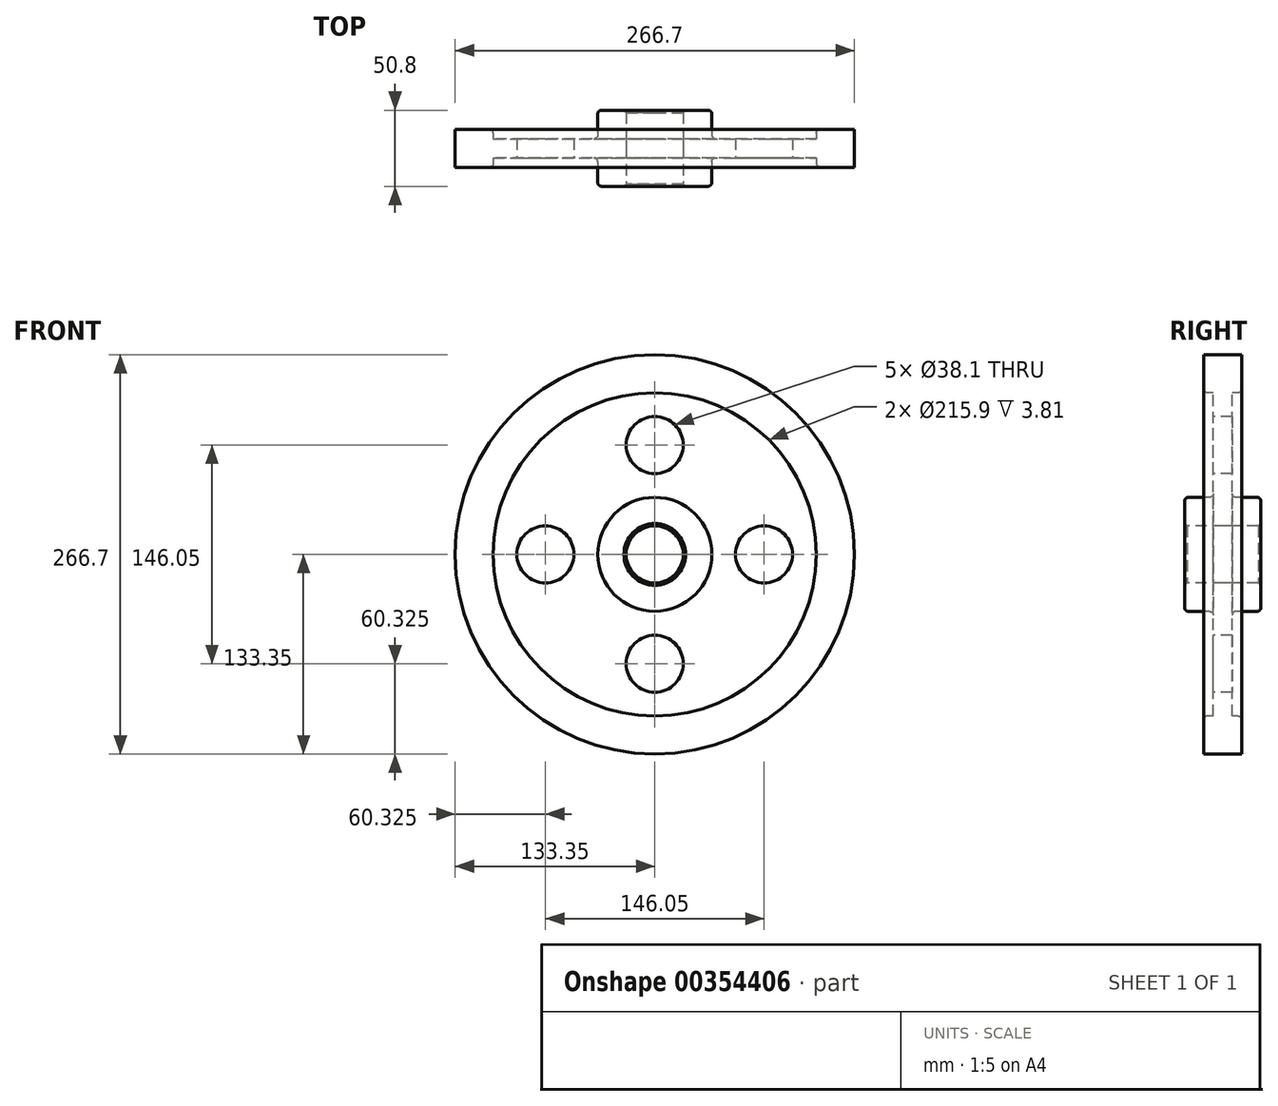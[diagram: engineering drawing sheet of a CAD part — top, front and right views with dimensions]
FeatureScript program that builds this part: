
annotation { "Feature Type Name" : "Feature", "Feature Type Description" : "" }
export const myFeature = defineFeature(function(context is Context, id is Id, definition is map)
    precondition{}
    {
        {
            var Q0;
            Q0=qCreatedBy(makeId("Right.planeOp"),FACE);
            var sketch = newSketch(context, id + "F0", { "sketchPlane" : qUnion([Q0])});
            skLineSegment(sketch, "E0", {"start": v(0, 0) * mm, "end": v(88.9, 0) * mm, "construction": true});
            skLineSegment(sketch, "E1.0", {"start": v(0, 19.05) * mm, "end": v(25.4, 19.05) * mm});
            skLineSegment(sketch, "E2.0", {"start": v(6.35, 38.1) * mm, "end": v(25.4, 38.1) * mm});
            skLineSegment(sketch, "E3.0", {"start": v(6.35, 107.95) * mm, "end": v(12.7, 107.95) * mm});
            skLineSegment(sketch, "E4.0", {"start": v(0, 133.35) * mm, "end": v(12.7, 133.35) * mm});
            skLineSegment(sketch, "E5", {"start": v(0, 133.35) * mm, "end": v(0, 0) * mm, "construction": true});
            skLineSegment(sketch, "E6.0", {"start": v(25.4, 38.1) * mm, "end": v(25.4, 19.05) * mm});
            skLineSegment(sketch, "E7.0", {"start": v(12.7, 133.35) * mm, "end": v(12.7, 107.95) * mm});
            skLineSegment(sketch, "E8.0", {"start": v(6.35, 107.95) * mm, "end": v(6.35, 38.1) * mm});
            skLineSegment(sketch, "E9.MirrorCS", {"start": v(0, 133.35) * mm, "end": v(-12.7, 133.35) * mm});
            skLineSegment(sketch, "E10.MirrorCS", {"start": v(-12.7, 133.35) * mm, "end": v(-12.7, 107.95) * mm});
            skLineSegment(sketch, "E11.MirrorCS", {"start": v(-6.35, 107.95) * mm, "end": v(-6.35, 38.1) * mm});
            skLineSegment(sketch, "E12.MirrorCS", {"start": v(-6.35, 38.1) * mm, "end": v(-25.4, 38.1) * mm});
            skLineSegment(sketch, "E13.MirrorCS", {"start": v(-25.4, 38.1) * mm, "end": v(-25.4, 19.05) * mm});
            skLineSegment(sketch, "E14.MirrorCS", {"start": v(0, 19.05) * mm, "end": v(-25.4, 19.05) * mm});
            skLineSegment(sketch, "E15.MirrorCS", {"start": v(0, 0) * mm, "end": v(-88.9, 0) * mm, "construction": true});
            skLineSegment(sketch, "E16", {"start": v(-6.35, 107.95) * mm, "end": v(-12.7, 107.95) * mm});
            skSolve(sketch);
        }
        {
            var Q0;
            Q0=makeQuery(id+"F0.imprint","IMPRINT",FACE,{"disambiguationData":[TD([[makeQuery(id+"F0.imprint","IMPRINT",EDGE,{"derivedFrom":sQuery(id+"F0.wireOp",EDGE,"E1.0")}),1.0]])]});
            var Q1;
            Q1=sQuery(id+"F0.wireOp",EDGE,"E0");
            revolve(context, id + "F1", {"entities" : qUnion([Q0]), "axis" : qUnion([Q1]), "revolveType" : RevolveType.FULL});
        }
        {
            var Q0;
            Q0=makeQuery(id+"F1.opRevolve","SWEPT_FACE",FACE,{"disambiguationData":[OSD([sQuery(id+"F0.wireOp",EDGE,"E11.MirrorCS")])]});
            var sketch = newSketch(context, id + "F2", { "sketchPlane" : qUnion([Q0])});
            skLineSegment(sketch, "E17", {"start": v(0, 0) * mm, "end": v(0, 73.03) * mm});
            skCircle(sketch, "E18", {"center": v(0, 73.03) * mm, "radius": 19.05 * mm});
            skCircle(sketch, "E19.1.0", {"center": v(-73.03, 0) * mm, "radius": 19.05 * mm});
            skCircle(sketch, "E19.2.0", {"center": v(0, -73.03) * mm, "radius": 19.05 * mm});
            skCircle(sketch, "E19.3.0", {"center": v(73.03, 0) * mm, "radius": 19.05 * mm});
            skPoint(sketch, "E19.center", {"position": v(0, 0) * mm});
            skSolve(sketch);
        }
        {
            var Q0;
            Q0=makeQuery(id+"F2.imprint","IMPRINT",FACE,{"disambiguationData":[TD([[makeQuery(id+"F2.imprint","IMPRINT",EDGE,{"derivedFrom":sQuery(id+"F2.wireOp",EDGE,"E19.3.0")}),1.0]])]});
            var Q1;
            Q1=makeQuery(id+"F2.imprint","IMPRINT",FACE,{"disambiguationData":[TD([[makeQuery(id+"F2.imprint","IMPRINT",EDGE,{"derivedFrom":sQuery(id+"F2.wireOp",EDGE,"E19.2.0")}),1.0]])]});
            var Q2;
            Q2=makeQuery(id+"F2.imprint","IMPRINT",FACE,{"disambiguationData":[TD([[makeQuery(id+"F2.imprint","IMPRINT",EDGE,{"derivedFrom":sQuery(id+"F2.wireOp",EDGE,"E18")}),1.0]])]});
            var Q3;
            Q3=makeQuery(id+"F2.imprint","IMPRINT",FACE,{"disambiguationData":[TD([[makeQuery(id+"F2.imprint","IMPRINT",EDGE,{"derivedFrom":sQuery(id+"F2.wireOp",EDGE,"E19.1.0")}),1.0]])]});
            extrude(context, id + "F3", {"entities" : qUnion([Q0, Q1, Q2, Q3]), "operationType" : NewBodyOperationType.REMOVE, "oppositeDirection" : true, "depth" : 25.4 * mm});
        }
        {
            var Q0;
            Q0=makeQuery(id+"F1.opRevolve","SWEPT_EDGE",EDGE,{"disambiguationData":[OSD([sQuery(id+"F0.wireOp",EDGE,"E10.MirrorCS"),sQuery(id+"F0.wireOp",EDGE,"E16")])]});
            var Q1;
            Q1=makeQuery(id+"F1.opRevolve","SWEPT_EDGE",EDGE,{"disambiguationData":[OSD([sQuery(id+"F0.wireOp",EDGE,"E11.MirrorCS"),sQuery(id+"F0.wireOp",EDGE,"E12.MirrorCS")])]});
            var Q2;
            Q2=makeQuery(id+"F1.opRevolve","SWEPT_EDGE",EDGE,{"disambiguationData":[OSD([sQuery(id+"F0.wireOp",EDGE,"E2.0"),sQuery(id+"F0.wireOp",EDGE,"E8.0")])]});
            var Q3;
            Q3=makeQuery(id+"F1.opRevolve","SWEPT_EDGE",EDGE,{"disambiguationData":[OSD([sQuery(id+"F0.wireOp",EDGE,"E3.0"),sQuery(id+"F0.wireOp",EDGE,"E7.0")])]});
            var Q4;
            Q4=makeQuery(id+"F1.opRevolve","SWEPT_EDGE",EDGE,{"disambiguationData":[OSD([sQuery(id+"F0.wireOp",EDGE,"E2.0"),sQuery(id+"F0.wireOp",EDGE,"E6.0")])]});
            var Q5;
            Q5=makeQuery(id+"F1.opRevolve","SWEPT_EDGE",EDGE,{"disambiguationData":[OSD([sQuery(id+"F0.wireOp",EDGE,"E12.MirrorCS"),sQuery(id+"F0.wireOp",EDGE,"E13.MirrorCS")])]});
            fillet(context, id + "F4", {"entities" : qUnion([Q0, Q1, Q2, Q3, Q4, Q5]), "radius" : 2.54 * mm, "tangentPropagation" : true, "allowEdgeOverflow" : false});
        }
        {
            var Q0;
            Q0=makeQuery(id+"F1.opRevolve","SWEPT_EDGE",EDGE,{"disambiguationData":[OSD([sQuery(id+"F0.wireOp",EDGE,"E13.MirrorCS"),sQuery(id+"F0.wireOp",EDGE,"E14.MirrorCS")])]});
            var Q1;
            Q1=makeQuery(id+"F1.opRevolve","SWEPT_EDGE",EDGE,{"disambiguationData":[OSD([sQuery(id+"F0.wireOp",EDGE,"E1.0"),sQuery(id+"F0.wireOp",EDGE,"E6.0")])]});
            chamfer(context, id + "F5", {"entities" : qUnion([Q0, Q1]), "width" : 1.59 * mm, "tangentPropagation" : true});
        }
    });
